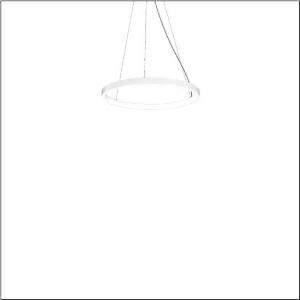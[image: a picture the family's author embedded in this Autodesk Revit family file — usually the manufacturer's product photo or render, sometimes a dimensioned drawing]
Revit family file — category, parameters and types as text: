
# Revit family: silica_r__21_ring-i_5pjbi1d3004a_1a46
name_source: partatom
category: Lighting Fixtures
units: mm (PartAtom-declared; Revit-internal decimal feet)

## family parameters
Cut with Voids When Loaded = No
Host = Face
Light Source = No
Part Type = Normal
Room Calculation Point = No
Round Connector Dimension = Use Diameter
Shared = No

## types (1)
- Silica® 21 Ring-I (1 x LED, 3510 lm, 60 W, 4000K)
    Apparent Load = 60 VA
    CIE Flux Codes = 22 48 76 50 101
    Color Rendering = 80
    Color Temperature = 4000K
    Default Elevation = 1800 mm
    Description = Silica® 21 Ring-I, suspended luminaire, of PMMA, frosted, light emission: inner ring side luminous distribution, primary light characteristic: symmetric, installation type: suspended mounting, LED, rated luminous flux: 3.510lm, luminous efficacy: 59lm/W, light colour: 840, colour temperature: 4000K, control gear: DALI 2, with terminal, 5-pole, mains connection: 230V, AC/DC, 0/50..60Hz, rated input power: 60W, housing, of extruded aluminium section, traffic white (RAL 9016), diameter: 610mm, ceiling canopy, traffic white (RAL 9016), protection rating (lamp compartment): IP40, insulation class (complete): insulation class I (protective earthing), certification: CE, impact resistance: IK02, permissible operating ambient temperature: 0..+35°C, packaging unit: 1 piece
    Height = 48 mm  [stored 0.15748 ft]
    Lamp = 1 x LED
    Lamp Light Flux = 3510 lm
    Lamp Power = 60 W
    Lamp count = 1
    Length = 610 mm
    Luminous efficacy = 59 lm/W
    Manufacturer = Siteco
    ModVariant = No
    Model = 5PJBI1D3004A
    Mounting Place = Ceiling
    Mounting Type = Pendant
    Number of Poles = 1
    OnlyDefault = Yes
    Power Factor = 1
    Product Name = Silica® 21 Ring-I
    Product group = suspended luminaire
    ProductGroupID = 905
    Protection Class = Protection class I
    Protection Degree = IP 40
    RLX_Detail_Level = 1
    RLX_Emergency_Light_Flux = 0 lm
    RLX_Emergency_Type = 0
    RLX_Emergency_Type_DB = No
    RlxData = <blob elided: 10509 chars, md5=0efbbb92>
    Socket = socket
    Standby Power = 0 W
    System Light Flux = 3510 lm
    System Power = 60 W
    Type Comments = Product without accessories
    Type Image = l_1258363.jpg
    URL = http://relux.com
    VarID = ---
    Voltage = 0 V
    Weight = 0.00 kg
    Width = 0 mm  [stored 0 ft]

note: [stored X ft] marks values corroborated as IEEE doubles in the binary element streams (Revit-internal decimal feet)

## geometry (parser evidence)
native form markers: Sweep x12
no freeform markers — native parametric forms only
